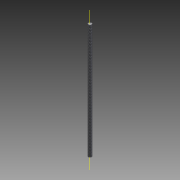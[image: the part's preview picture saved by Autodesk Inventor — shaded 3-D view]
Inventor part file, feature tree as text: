
AUTODESK INVENTOR PART (.ipt)
format: ipt  version: 2013 (Build 170138000, 138)  size: 66,048 bytes
history: native  units: in
note: dims shown in document units (in); Inventor stores cm internally (conversion verified against a paired STEP export)
features: extrude x1, thread x1, other x1, sketch x1
ambient origin geometry x8: Origin, YZ Plane, XZ Plane, XY Plane, X Axis, Y Axis, Z Axis, Center Point
bodies: Solid1 (feature_tree)
feature tree (4):
  extrude  "Extrusion1"  Depth=18.0in TaperAngle=0.0deg
  thread  "Thread1"  [1 undecoded]
  other  "Work Axis1"
  sketch  "Sketch1"  dims[d0=0.5in d2=18.0in d3=0.0in d4=1.0in d5=0.0in]
note: 1 required parameter value undecoded (feature->parameter linkage not recoverable at this tier; creation-order binding heuristic only, values carry confidence <= 0.55)
